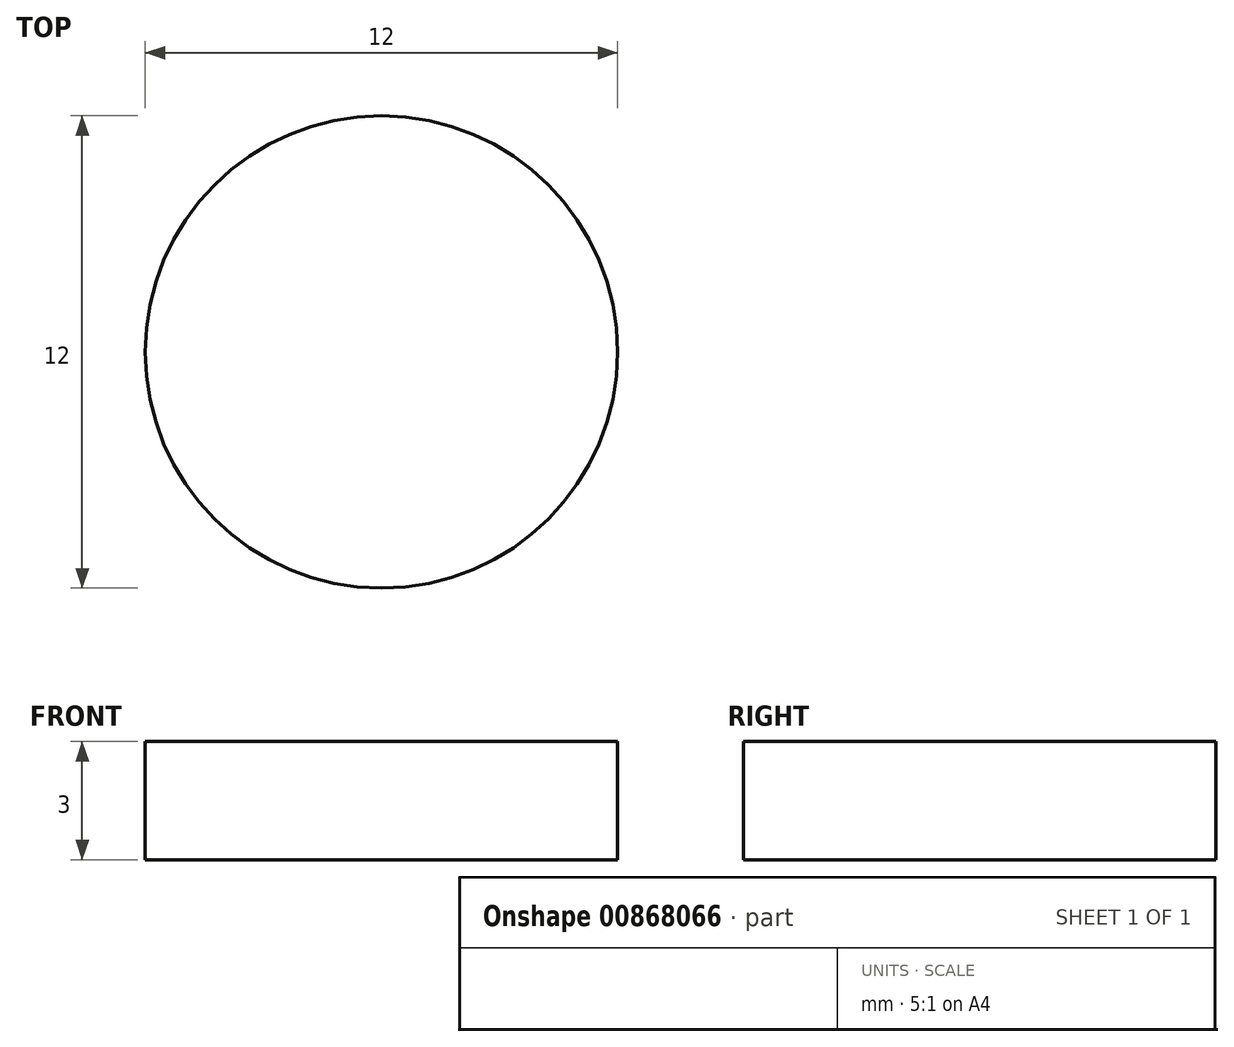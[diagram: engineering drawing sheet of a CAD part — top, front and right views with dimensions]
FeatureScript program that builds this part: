
annotation { "Feature Type Name" : "Feature", "Feature Type Description" : "" }
export const myFeature = defineFeature(function(context is Context, id is Id, definition is map)
    precondition{}
    {
        {
            var Q0;
            Q0=qCreatedBy(makeId("Top.planeOp"),FACE);
            var sketch = newSketch(context, id + "F0", { "sketchPlane" : qUnion([Q0])});
            skCircle(sketch, "E0", {"center": v(0, 0) * mm, "radius": 6 * mm});
            skSolve(sketch);
        }
        {
            var Q0;
            Q0 = qSketchRegion(id + "F0", true);
            extrude(context, id + "F1", {"entities" : qUnion([Q0]), "depth" : 3 * mm, "offsetDistance" : 25 * mm});
        }
    });
